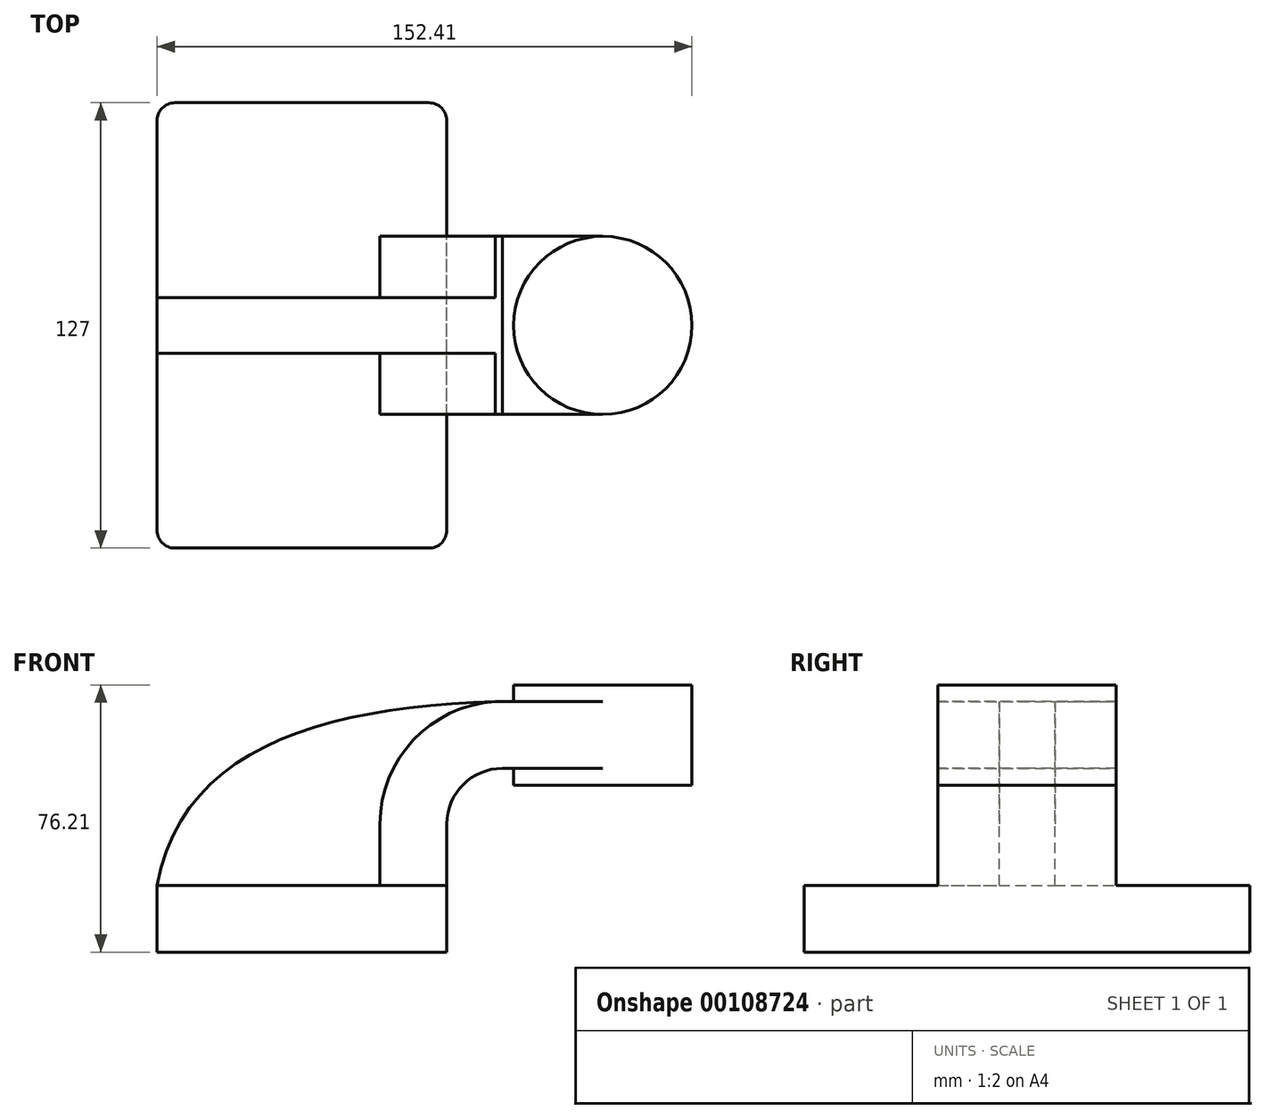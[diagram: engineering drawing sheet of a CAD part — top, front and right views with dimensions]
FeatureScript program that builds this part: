
annotation { "Feature Type Name" : "Feature", "Feature Type Description" : "" }
export const myFeature = defineFeature(function(context is Context, id is Id, definition is map)
    precondition{}
    {
        {
            var Q0;
            Q0=qCreatedBy(makeId("Front.planeOp"),FACE);
            var sketch = newSketch(context, id + "F0", { "sketchPlane" : qUnion([Q0])});
            skLineSegment(sketch, "E0.bottom", {"start": v(41.28, -9.52) * mm, "end": v(-41.27, -9.52) * mm});
            skLineSegment(sketch, "E0.top", {"start": v(41.27, 9.53) * mm, "end": v(-41.28, 9.53) * mm});
            skLineSegment(sketch, "E0.left", {"start": v(41.28, -9.52) * mm, "end": v(41.28, 9.52) * mm});
            skLineSegment(sketch, "E0.right", {"start": v(-41.27, -9.52) * mm, "end": v(-41.28, 9.52) * mm});
            skPoint(sketch, "E0.middle", {"position": v(0, 0) * mm});
            skLineSegment(sketch, "E1.bottom", {"start": v(111.12, 38.1) * mm, "end": v(60.33, 38.1) * mm});
            skLineSegment(sketch, "E1.top", {"start": v(111.12, 66.68) * mm, "end": v(60.33, 66.68) * mm});
            skLineSegment(sketch, "E1.left", {"start": v(111.13, 38.1) * mm, "end": v(111.12, 66.68) * mm});
            skLineSegment(sketch, "E1.right", {"start": v(60.33, 38.1) * mm, "end": v(60.33, 66.68) * mm});
            skPoint(sketch, "E1.middle", {"position": v(85.72, 52.39) * mm});
            skLineSegment(sketch, "E2", {"start": v(41.27, 9.53) * mm, "end": v(41.27, 27) * mm});
            skArc(sketch, "E3", {"start": v(41.28, 27) * mm, "mid": v(45.92, 38.23) * mm, "end": v(57.15, 42.88) * mm});
            skLineSegment(sketch, "E4", {"start": v(57.15, 42.88) * mm, "end": v(85.72, 42.88) * mm});
            skLineSegment(sketch, "E5.0", {"start": v(57.15, 61.93) * mm, "end": v(85.72, 61.93) * mm});
            skArc(sketch, "E5.1", {"start": v(22.23, 27) * mm, "mid": v(32.45, 51.7) * mm, "end": v(57.15, 61.93) * mm});
            skLineSegment(sketch, "E5.2", {"start": v(22.23, 9.53) * mm, "end": v(22.23, 27) * mm});
            skFitSpline(sketch, "E6", {"points": [v(-41.28, 9.52) * mm, v(57.15, 61.93) * mm], "startDerivative": vector(22.3, 121.46) * mm, "endDerivative": vector(147.4, 3.94) * mm});
            skLineSegment(sketch, "E7", {"start": v(85.72, 38.1) * mm, "end": v(85.72, 66.68) * mm});
            skSolve(sketch);
        }
        {
            var Q0;
            Q0=makeQuery(id+"F0.imprint","IMPRINT",FACE,{"disambiguationData":[TD([[makeQuery(id+"F0.imprint","IMPRINT",EDGE,{"derivedFrom":sQuery(id+"F0.wireOp",EDGE,"E0.bottom")}),-1.0]])]});
            extrude(context, id + "F1", {"entities" : qUnion([Q0]), "endBound" : BoundingType.SYMMETRIC, "depth" : 127 * mm});
        }
        {
            var Q0;
            {var subQ3=sQuery(id+"F0.wireOp",EDGE,"E5.2");Q0=makeQuery(id+"F0.imprint","IMPRINT",FACE,{"disambiguationData":[TD([[makeQuery(id+"F0.imprint","IMPRINT",EDGE,{"derivedFrom":subQ3}),1.0]])]});}
            extrude(context, id + "F2", {"entities" : qUnion([Q0]), "operationType" : NewBodyOperationType.ADD, "endBound" : BoundingType.SYMMETRIC, "depth" : 15.88 * mm});
        }
        {
            var Q0;
            {var subQ0=sQuery(id+"F0.wireOp",EDGE,"E2");Q0=makeQuery(id+"F0.imprint","IMPRINT",FACE,{"disambiguationData":[TD([[makeQuery(id+"F0.imprint","IMPRINT",EDGE,{"derivedFrom":subQ0}),1.0]])]});}
            var Q1;
            {var subQ0=sQuery(id+"F0.wireOp",EDGE,"E4");var subQ1=sQuery(id+"F0.wireOp",EDGE,"E1.right");var subQ2=makeQuery(id+"F0.imprint","INTERSECT",VERTEX,{"derivedFrom":[subQ1,subQ0]});Q1=makeQuery(id+"F0.imprint","IMPRINT",FACE,{"disambiguationData":[TD([[makeQuery(id+"F0.imprint","IMPRINT",EDGE,{"disambiguationData":[TD([[subQ2,-1.0]])],"derivedFrom":subQ1}),-1.0]])]});}
            extrude(context, id + "F3", {"entities" : qUnion([Q0, Q1]), "operationType" : NewBodyOperationType.ADD, "endBound" : BoundingType.SYMMETRIC, "depth" : 50.8 * mm});
        }
        {
            var Q0;
            {var subQ4=sQuery(id+"F0.wireOp",EDGE,"E1.left");Q0=makeQuery(id+"F0.imprint","IMPRINT",FACE,{"disambiguationData":[TD([[makeQuery(id+"F0.imprint","IMPRINT",EDGE,{"derivedFrom":subQ4}),1.0]])]});}
            var Q1;
            Q1=sQuery(id+"F0.wireOp",EDGE,"E7");
            revolve(context, id + "F4", {"operationType" : NewBodyOperationType.ADD, "entities" : qUnion([Q0]), "axis" : qUnion([Q1]), "revolveType" : RevolveType.FULL});
        }
        {
            var Q0;
            Q0=makeQuery(id+"F1.opExtrude","CAP_EDGE",EDGE,{"disambiguationData":[OSD([sQuery(id+"F0.wireOp",EDGE,"E0.right")])],"isStart":false});
            var Q1;
            Q1=makeQuery(id+"F1.opExtrude","CAP_EDGE",EDGE,{"disambiguationData":[OSD([sQuery(id+"F0.wireOp",EDGE,"E0.left")])],"isStart":false});
            var Q2;
            Q2=makeQuery(id+"F1.opExtrude","CAP_EDGE",EDGE,{"disambiguationData":[OSD([sQuery(id+"F0.wireOp",EDGE,"E0.right")])],"isStart":true});
            var Q3;
            Q3=makeQuery(id+"F1.opExtrude","CAP_EDGE",EDGE,{"disambiguationData":[OSD([sQuery(id+"F0.wireOp",EDGE,"E0.left")])],"isStart":true});
            fillet(context, id + "F5", {"entities" : qUnion([Q0, Q1, Q2, Q3]), "radius" : 5.08 * mm, "tangentPropagation" : true, "allowEdgeOverflow" : false});
        }
    });
